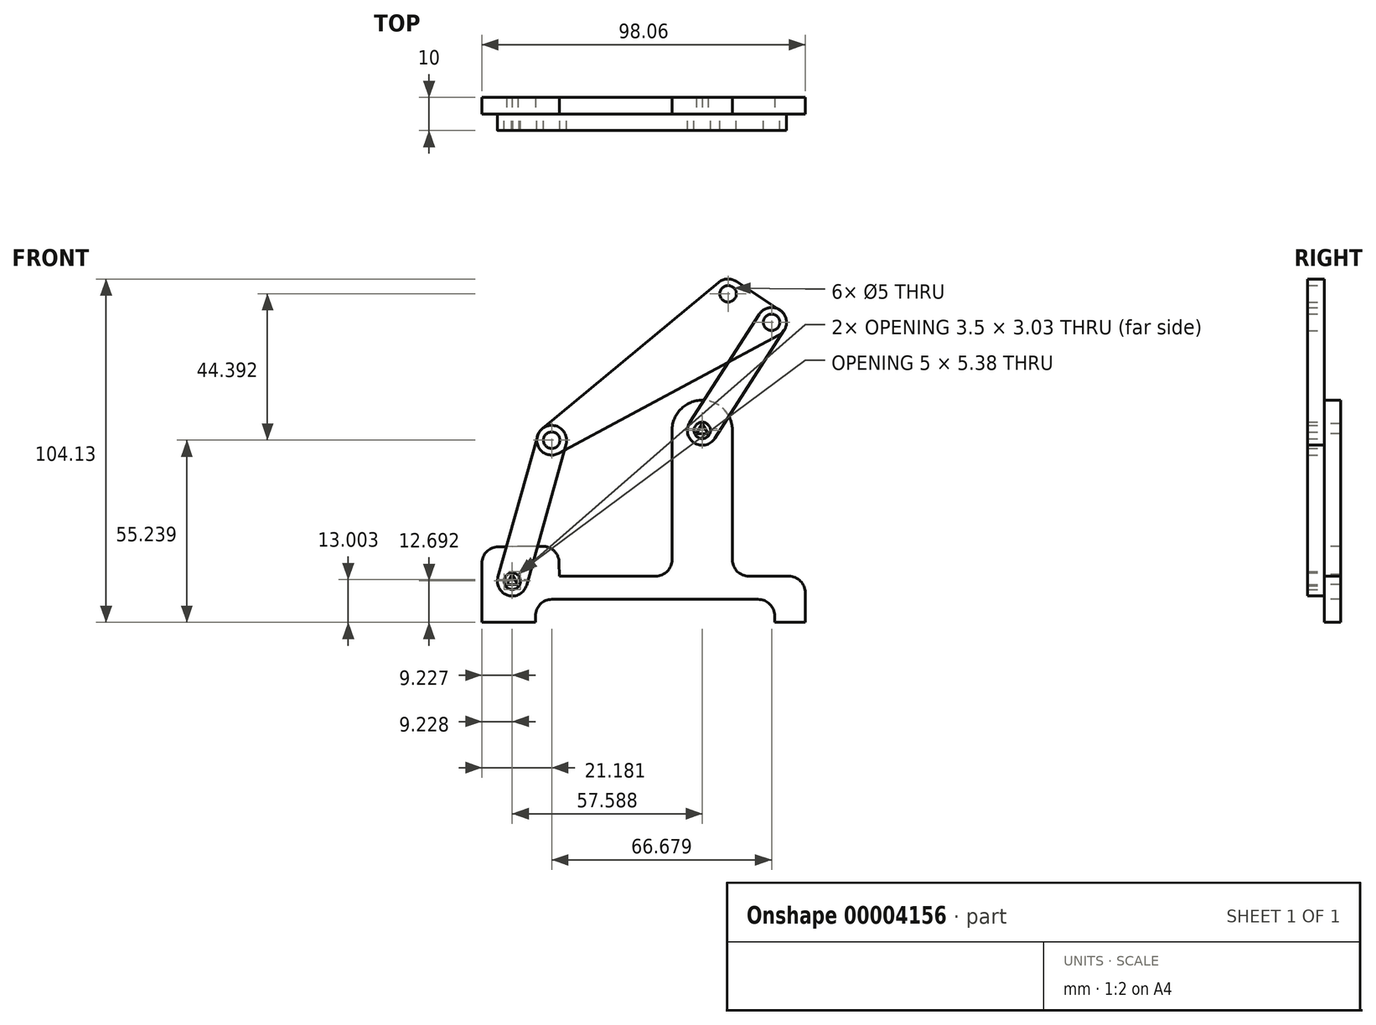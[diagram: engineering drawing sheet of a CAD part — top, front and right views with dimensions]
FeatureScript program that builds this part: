
annotation { "Feature Type Name" : "Feature", "Feature Type Description" : "" }
export const myFeature = defineFeature(function(context is Context, id is Id, definition is map)
    precondition{}
    {
        {
            var Q0;
            Q0=qCreatedBy(makeId("Front.planeOp"),FACE);
            var sketch = newSketch(context, id + "F0", { "sketchPlane" : qUnion([Q0])});
            skLineSegment(sketch, "E0", {"start": v(0, 0) * mm, "end": v(16.8, 0) * mm, "construction": true});
            skLineSegment(sketch, "E1", {"start": v(16.8, 0) * mm, "end": v(16.8, 25.09) * mm, "construction": true});
            skPoint(sketch, "E2", {"position": v(16.8, 25.09) * mm});
            skLineSegment(sketch, "E3", {"start": v(0, 0) * mm, "end": v(43.91, 0) * mm, "construction": true});
            skLineSegment(sketch, "E4", {"start": v(43.91, 0) * mm, "end": v(43.91, 53.03) * mm, "construction": true});
            skPoint(sketch, "E5", {"position": v(43.91, 53.03) * mm});
            skLineSegment(sketch, "E6", {"start": v(0, 0) * mm, "end": v(-40.78, 0) * mm, "construction": true});
            skLineSegment(sketch, "E7", {"start": v(-40.78, -20.63) * mm, "end": v(-40.78, 0) * mm, "construction": true});
            skLineSegment(sketch, "E8", {"start": v(0, 0) * mm, "end": v(-24.45, 0) * mm, "construction": true});
            skLineSegment(sketch, "E9", {"start": v(-24.45, 20.63) * mm, "end": v(-24.45, 0) * mm, "construction": true});
            skLineSegment(sketch, "E10", {"start": v(0, 0) * mm, "end": v(31.16, 0) * mm, "construction": true});
            skLineSegment(sketch, "E11", {"start": v(31.16, 0) * mm, "end": v(31.16, 62.33) * mm, "construction": true});
            skPoint(sketch, "E12", {"position": v(31.16, 62.33) * mm});
            skPoint(sketch, "E13", {"position": v(-24.45, 20.63) * mm});
            skPoint(sketch, "E14", {"position": v(-40.78, -20.63) * mm});
            skSolve(sketch);
        }
        {
            var Q0;
            Q0=qCreatedBy(makeId("Front.planeOp"),FACE);
            var sketch = newSketch(context, id + "F1", { "sketchPlane" : qUnion([Q0])});
            skPoint(sketch, "E15.0", {"position": v(31.16, 62.33) * mm});
            skPoint(sketch, "E16.0", {"position": v(43.91, 53.03) * mm});
            skPoint(sketch, "E17.0", {"position": v(16.8, 25.09) * mm});
            skPoint(sketch, "E18.0", {"position": v(-24.45, 20.63) * mm});
            skPoint(sketch, "E19.0", {"position": v(-40.78, -20.63) * mm});
            skCircle(sketch, "E20", {"center": v(43.91, 53.03) * mm, "radius": 5 * mm});
            skCircle(sketch, "E21", {"center": v(31.16, 62.33) * mm, "radius": 5 * mm});
            skCircle(sketch, "E22", {"center": v(16.8, 25.09) * mm, "radius": 5 * mm});
            skCircle(sketch, "E23", {"center": v(-24.45, 20.63) * mm, "radius": 5 * mm});
            skCircle(sketch, "E24", {"center": v(-40.78, -20.63) * mm, "radius": 5 * mm});
            skCircle(sketch, "E25", {"center": v(-40.78, -20.63) * mm, "radius": 3 * mm});
            skCircle(sketch, "E26", {"center": v(-24.45, 20.63) * mm, "radius": 3 * mm});
            skCircle(sketch, "E27", {"center": v(16.8, 25.09) * mm, "radius": 3 * mm});
            skCircle(sketch, "E28", {"center": v(43.91, 53.03) * mm, "radius": 3 * mm});
            skCircle(sketch, "E29", {"center": v(31.16, 62.33) * mm, "radius": 3 * mm});
            skLineSegment(sketch, "E30", {"start": v(46.86, 57.07) * mm, "end": v(34.1, 66.37) * mm});
            skLineSegment(sketch, "E31", {"start": v(28.16, 66.33) * mm, "end": v(-27.45, 24.63) * mm});
            skLineSegment(sketch, "E32", {"start": v(46.06, 48.51) * mm, "end": v(-22.3, 16.11) * mm});
            skLineSegment(sketch, "E33", {"start": v(20.4, 21.6) * mm, "end": v(47.5, 49.55) * mm});
            skLineSegment(sketch, "E34", {"start": v(40.33, 56.51) * mm, "end": v(13.22, 28.57) * mm});
            skLineSegment(sketch, "E35", {"start": v(-19.8, 18.8) * mm, "end": v(-36.13, -22.47) * mm});
            skLineSegment(sketch, "E36", {"start": v(-29.1, 22.47) * mm, "end": v(-46.2, -20.74) * mm});
            skCircle(sketch, "E37.0", {"center": v(16.8, 25.09) * mm, "radius": 10 * mm});
            skCircle(sketch, "E38.0", {"center": v(-24.45, 20.63) * mm, "radius": 10 * mm});
            skLineSegment(sketch, "E39", {"start": v(17.65, 35.05) * mm, "end": v(-25.48, 30.58) * mm});
            skLineSegment(sketch, "E40", {"start": v(25.88, 29.3) * mm, "end": v(52.76, -28.66) * mm});
            skLineSegment(sketch, "E41", {"start": v(48.23, -35.77) * mm, "end": v(-67.2, -35.77) * mm});
            skLineSegment(sketch, "E42", {"start": v(-71.28, -27.87) * mm, "end": v(-32.6, 26.44) * mm});
            skPoint(sketch, "E43.visualSharp", {"position": v(56.06, -35.77) * mm});
            skArc(sketch, "E43.filletArc", {"start": v(48.23, -35.77) * mm, "mid": v(52.44, -33.46) * mm, "end": v(52.76, -28.66) * mm});
            skPoint(sketch, "E44.visualSharp", {"position": v(-76.9, -35.77) * mm});
            skArc(sketch, "E44.filletArc", {"start": v(-71.28, -27.87) * mm, "mid": v(-71.65, -33.06) * mm, "end": v(-67.2, -35.77) * mm});
            skSolve(sketch);
        }
        {
            var Q0;
            Q0=qCreatedBy(makeId("Front.planeOp"),FACE);
            var sketch = newSketch(context, id + "F2", { "sketchPlane" : qUnion([Q0])});
            skPoint(sketch, "E45.0", {"position": v(24.65, 66.5) * mm});
            skPoint(sketch, "E46.0", {"position": v(37.85, 57.84) * mm});
            skPoint(sketch, "E47.0", {"position": v(16.8, 25.09) * mm});
            skPoint(sketch, "E48.0", {"position": v(-40.78, -20.63) * mm});
            skLineSegment(sketch, "E49", {"start": v(37.85, 57.84) * mm, "end": v(24.65, 66.5) * mm, "construction": true});
            skLineSegment(sketch, "E50", {"start": v(24.65, 66.5) * mm, "end": v(-28.83, 22.1) * mm, "construction": true});
            skLineSegment(sketch, "E51", {"start": v(-28.83, 22.1) * mm, "end": v(37.85, 57.84) * mm, "construction": true});
            skLineSegment(sketch, "E52", {"start": v(37.85, 57.84) * mm, "end": v(16.8, 25.09) * mm, "construction": true});
            skLineSegment(sketch, "E53", {"start": v(-28.83, 22.1) * mm, "end": v(-40.78, -20.63) * mm, "construction": true});
            skSolve(sketch);
        }
        {
            var Q0;
            Q0=qCreatedBy(makeId("Front.planeOp"),FACE);
            var sketch = newSketch(context, id + "F3", { "sketchPlane" : qUnion([Q0])});
            skPoint(sketch, "E54.0", {"position": v(16.8, 25.09) * mm});
            skPoint(sketch, "E55.0", {"position": v(24.65, 66.5) * mm});
            skPoint(sketch, "E56.0", {"position": v(-28.83, 22.1) * mm});
            skPoint(sketch, "E57.0", {"position": v(-40.78, -20.63) * mm});
            skCircle(sketch, "E58", {"center": v(24.65, 66.5) * mm, "radius": 2.5 * mm});
            skCircle(sketch, "E59", {"center": v(24.65, 66.5) * mm, "radius": 4.5 * mm});
            skCircle(sketch, "E60", {"center": v(-28.83, 22.1) * mm, "radius": 4.5 * mm});
            skCircle(sketch, "E61", {"center": v(-28.83, 22.1) * mm, "radius": 2.5 * mm});
            skCircle(sketch, "E62", {"center": v(-40.78, -20.63) * mm, "radius": 2.5 * mm});
            skCircle(sketch, "E63", {"center": v(16.8, 25.09) * mm, "radius": 2.5 * mm});
            skPoint(sketch, "E64.0", {"position": v(37.85, 57.84) * mm});
            skCircle(sketch, "E65", {"center": v(37.85, 57.84) * mm, "radius": 2.5 * mm});
            skCircle(sketch, "E66", {"center": v(37.85, 57.84) * mm, "radius": 4.5 * mm});
            skCircle(sketch, "E67", {"center": v(16.8, 25.09) * mm, "radius": 4.5 * mm});
            skCircle(sketch, "E68", {"center": v(-40.78, -20.63) * mm, "radius": 4.5 * mm});
            skLineSegment(sketch, "E69", {"start": v(48.05, -33.13) * mm, "end": v(38.76, -33.13) * mm});
            skLineSegment(sketch, "E70", {"start": v(38.76, -33.13) * mm, "end": v(38.76, -31.13) * mm});
            skLineSegment(sketch, "E71", {"start": v(33.76, -26.13) * mm, "end": v(-28.76, -26.13) * mm});
            skLineSegment(sketch, "E72", {"start": v(-33.76, -31.13) * mm, "end": v(-33.76, -33.13) * mm});
            skLineSegment(sketch, "E73.trimOffspring", {"start": v(-33.76, -33.13) * mm, "end": v(-50.01, -33.13) * mm});
            skLineSegment(sketch, "E74", {"start": v(-24.5, 20.9) * mm, "end": v(-36.45, -21.84) * mm});
            skLineSegment(sketch, "E75", {"start": v(-33.16, 23.32) * mm, "end": v(-45.12, -19.42) * mm});
            skLineSegment(sketch, "E76", {"start": v(-26.7, 18.14) * mm, "end": v(39.97, 53.87) * mm});
            skLineSegment(sketch, "E77", {"start": v(21.78, 69.96) * mm, "end": v(-31.7, 25.57) * mm});
            skLineSegment(sketch, "E78", {"start": v(40.32, 61.6) * mm, "end": v(27.12, 70.26) * mm});
            skLineSegment(sketch, "E79", {"start": v(41.64, 55.4) * mm, "end": v(20.6, 22.65) * mm});
            skLineSegment(sketch, "E80", {"start": v(34.06, 60.27) * mm, "end": v(13.02, 27.52) * mm});
            skPoint(sketch, "E81.visualSharp", {"position": v(38.76, -26.13) * mm});
            skArc(sketch, "E81.filletArc", {"start": v(38.76, -31.13) * mm, "mid": v(37.3, -27.6) * mm, "end": v(33.76, -26.13) * mm});
            skPoint(sketch, "E82.visualSharp", {"position": v(-33.76, -26.13) * mm});
            skArc(sketch, "E82.filletArc", {"start": v(-28.76, -26.13) * mm, "mid": v(-32.3, -27.6) * mm, "end": v(-33.76, -31.13) * mm});
            skLineSegment(sketch, "E83", {"start": v(-45.06, -10.2) * mm, "end": v(-31.62, -10.06) * mm});
            skLineSegment(sketch, "E84", {"start": v(-26.57, -15.01) * mm, "end": v(-26.53, -19.12) * mm});
            skLineSegment(sketch, "E85", {"start": v(-26.53, -19.12) * mm, "end": v(2.66, -19.12) * mm});
            skLineSegment(sketch, "E86", {"start": v(7.66, -14.12) * mm, "end": v(7.66, 25.09) * mm});
            skLineSegment(sketch, "E87", {"start": v(25.95, 25.09) * mm, "end": v(25.95, -14.12) * mm});
            skLineSegment(sketch, "E88", {"start": v(30.95, -19.12) * mm, "end": v(43.05, -19.12) * mm});
            skArc(sketch, "E89", {"start": v(25.95, 25.09) * mm, "mid": v(16.8, 34.23) * mm, "end": v(7.66, 25.09) * mm});
            skPoint(sketch, "E90.visualSharp", {"position": v(-26.62, -10.01) * mm});
            skArc(sketch, "E90.filletArc", {"start": v(-26.57, -15.01) * mm, "mid": v(-28.07, -11.5) * mm, "end": v(-31.62, -10.06) * mm});
            skLineSegment(sketch, "E91", {"start": v(-50.01, -15.2) * mm, "end": v(-50.01, -33.13) * mm});
            skLineSegment(sketch, "E92", {"start": v(48.05, -24.12) * mm, "end": v(48.05, -33.13) * mm});
            skPoint(sketch, "E93.visualSharp", {"position": v(48.05, -19.12) * mm});
            skArc(sketch, "E93.filletArc", {"start": v(48.05, -24.12) * mm, "mid": v(46.59, -20.58) * mm, "end": v(43.05, -19.12) * mm});
            skPoint(sketch, "E94.visualSharp", {"position": v(-50.01, -10.25) * mm});
            skArc(sketch, "E94.filletArc", {"start": v(-45.06, -10.2) * mm, "mid": v(-48.57, -11.68) * mm, "end": v(-50.01, -15.2) * mm});
            skPoint(sketch, "E95.visualSharp", {"position": v(25.95, -19.12) * mm});
            skArc(sketch, "E95.filletArc", {"start": v(25.95, -14.12) * mm, "mid": v(27.41, -17.65) * mm, "end": v(30.95, -19.12) * mm});
            skPoint(sketch, "E96.visualSharp", {"position": v(7.66, -19.12) * mm});
            skArc(sketch, "E96.filletArc", {"start": v(2.66, -19.12) * mm, "mid": v(6.2, -17.65) * mm, "end": v(7.66, -14.12) * mm});
            skLineSegment(sketch, "E97", {"start": v(-38.28, -22.08) * mm, "end": v(-43.28, -22.08) * mm});
            skLineSegment(sketch, "E98", {"start": v(-43.28, -22.08) * mm, "end": v(-40.78, -17.75) * mm});
            skLineSegment(sketch, "E99", {"start": v(-40.78, -17.75) * mm, "end": v(-38.28, -22.08) * mm});
            skLineSegment(sketch, "E100", {"start": v(-40.78, -22.08) * mm, "end": v(-40.78, -17.75) * mm, "construction": true});
            skLineSegment(sketch, "E101", {"start": v(-39.53, -19.91) * mm, "end": v(-43.28, -22.08) * mm, "construction": true});
            skLineSegment(sketch, "E102", {"start": v(-42.03, -19.91) * mm, "end": v(-38.28, -22.08) * mm, "construction": true});
            skSolve(sketch);
        }
        {
            var Q0;
            Q0=qCreatedBy(makeId("Front.planeOp"),FACE);
            var sketch = newSketch(context, id + "F4", { "sketchPlane" : qUnion([Q0])});
            skArc(sketch, "E103.0", {"start": v(-45.06, -10.2) * mm, "mid": v(-48.57, -11.68) * mm, "end": v(-50.01, -15.2) * mm});
            skArc(sketch, "E103.2", {"start": v(-26.57, -15.01) * mm, "mid": v(-28.07, -11.5) * mm, "end": v(-31.62, -10.06) * mm});
            skLineSegment(sketch, "E103.3", {"start": v(-26.57, -15.01) * mm, "end": v(-26.53, -19.12) * mm});
            skLineSegment(sketch, "E104.0.0", {"start": v(48.05, -33.13) * mm, "end": v(38.76, -33.13) * mm});
            skLineSegment(sketch, "E104.0.1", {"start": v(48.05, -24.12) * mm, "end": v(48.05, -33.13) * mm});
            skArc(sketch, "E104.0.2", {"start": v(48.05, -24.12) * mm, "mid": v(46.59, -20.58) * mm, "end": v(43.05, -19.12) * mm});
            skLineSegment(sketch, "E104.0.3", {"start": v(30.95, -19.12) * mm, "end": v(43.05, -19.12) * mm});
            skArc(sketch, "E104.0.4", {"start": v(25.95, -14.12) * mm, "mid": v(27.41, -17.65) * mm, "end": v(30.95, -19.12) * mm});
            skLineSegment(sketch, "E104.0.5", {"start": v(25.95, 25.09) * mm, "end": v(25.95, -14.12) * mm});
            skLineSegment(sketch, "E104.0.11", {"start": v(7.66, -14.12) * mm, "end": v(7.66, 25.09) * mm});
            skArc(sketch, "E104.0.12", {"start": v(2.66, -19.12) * mm, "mid": v(6.2, -17.65) * mm, "end": v(7.66, -14.12) * mm});
            skLineSegment(sketch, "E104.0.13", {"start": v(-26.53, -19.12) * mm, "end": v(2.66, -19.12) * mm});
            skLineSegment(sketch, "E104.0.22", {"start": v(-50.01, -15.2) * mm, "end": v(-50.01, -33.13) * mm});
            skLineSegment(sketch, "E104.0.23", {"start": v(-33.76, -33.13) * mm, "end": v(-50.01, -33.13) * mm});
            skLineSegment(sketch, "E104.0.24", {"start": v(-33.76, -31.13) * mm, "end": v(-33.76, -33.13) * mm});
            skArc(sketch, "E104.0.25", {"start": v(-28.76, -26.13) * mm, "mid": v(-32.3, -27.6) * mm, "end": v(-33.76, -31.13) * mm});
            skLineSegment(sketch, "E104.0.26", {"start": v(33.76, -26.13) * mm, "end": v(-28.76, -26.13) * mm});
            skArc(sketch, "E104.0.27", {"start": v(38.76, -31.13) * mm, "mid": v(37.3, -27.6) * mm, "end": v(33.76, -26.13) * mm});
            skLineSegment(sketch, "E104.0.28", {"start": v(38.76, -33.13) * mm, "end": v(38.76, -31.13) * mm});
            skArc(sketch, "E105.0", {"start": v(25.95, 25.09) * mm, "mid": v(16.8, 34.23) * mm, "end": v(7.66, 25.09) * mm});
            skPoint(sketch, "E106", {"position": v(-40.78, -20.63) * mm});
            skLineSegment(sketch, "E107", {"start": v(-31.62, -10.06) * mm, "end": v(-45.06, -10.2) * mm});
            skLineSegment(sketch, "E108", {"start": v(-39.03, -21.64) * mm, "end": v(-42.53, -21.64) * mm});
            skLineSegment(sketch, "E109", {"start": v(-42.53, -21.64) * mm, "end": v(-40.78, -18.61) * mm});
            skLineSegment(sketch, "E110", {"start": v(-40.78, -18.61) * mm, "end": v(-39.03, -21.64) * mm});
            skLineSegment(sketch, "E111", {"start": v(-39.9, -20.13) * mm, "end": v(-42.53, -21.64) * mm, "construction": true});
            skLineSegment(sketch, "E112", {"start": v(-41.66, -20.13) * mm, "end": v(-39.03, -21.64) * mm, "construction": true});
            skLineSegment(sketch, "E113", {"start": v(-40.78, -18.61) * mm, "end": v(-40.78, -21.64) * mm, "construction": true});
            skLineSegment(sketch, "E114", {"start": v(18.56, 24.08) * mm, "end": v(15.06, 24.08) * mm});
            skLineSegment(sketch, "E115", {"start": v(15.06, 24.08) * mm, "end": v(16.8, 27.1) * mm});
            skLineSegment(sketch, "E116", {"start": v(16.8, 27.1) * mm, "end": v(18.56, 24.08) * mm});
            skLineSegment(sketch, "E117", {"start": v(16.8, 27.1) * mm, "end": v(16.8, 24.08) * mm, "construction": true});
            skLineSegment(sketch, "E118", {"start": v(17.68, 25.6) * mm, "end": v(15.06, 24.08) * mm, "construction": true});
            skLineSegment(sketch, "E119", {"start": v(15.93, 25.6) * mm, "end": v(18.56, 24.08) * mm, "construction": true});
            skSolve(sketch);
        }
        {
            var Q0;
            Q0=makeQuery(id+"F4.imprint","IMPRINT",FACE,{"disambiguationData":[TD([[makeQuery(id+"F4.imprint","IMPRINT",EDGE,{"derivedFrom":sQuery(id+"F4.wireOp",EDGE,"E104.0.0")}),-1.0]])]});
            extrude(context, id + "F5", {"entities" : qUnion([Q0]), "oppositeDirection" : true, "depth" : 5 * mm});
        }
        {
            var Q0;
            {var subQ3=sQuery(id+"F3.wireOp",EDGE,"E75");var subQ7=sQuery(id+"F3.wireOp",EDGE,"E60");var subQ9=makeQuery(id+"F3.imprint","INTERSECT",VERTEX,{"derivedFrom":[subQ7,subQ3]});Q0=makeQuery(id+"F3.imprint","IMPRINT",FACE,{"disambiguationData":[TD([[makeQuery(id+"F3.imprint","IMPRINT",EDGE,{"disambiguationData":[TD([[subQ9,-1.0]])],"derivedFrom":subQ7}),-1.0]])]});}
            var Q1;
            {var subQ1=sQuery(id+"F3.wireOp",EDGE,"E74");var subQ5=sQuery(id+"F3.wireOp",EDGE,"E68");var subQ7=makeQuery(id+"F3.imprint","INTERSECT",VERTEX,{"derivedFrom":[subQ5,subQ1]});Q1=makeQuery(id+"F3.imprint","IMPRINT",FACE,{"disambiguationData":[TD([[makeQuery(id+"F3.imprint","IMPRINT",EDGE,{"disambiguationData":[TD([[subQ7,-1.0]])],"derivedFrom":subQ5}),-1.0]])]});}
            var Q2;
            {var subQ1=sQuery(id+"F3.wireOp",EDGE,"E62");var subQ5=sQuery(id+"F3.wireOp",EDGE,"E98");var subQ15=makeQuery(id+"F3.imprint","INTERSECT",VERTEX,{"disambiguationData":[OD(0.0)],"derivedFrom":[subQ1,subQ5]});Q2=makeQuery(id+"F3.imprint","IMPRINT",FACE,{"disambiguationData":[TD([[makeQuery(id+"F3.imprint","IMPRINT",EDGE,{"disambiguationData":[TD([[subQ15,-1.0]])],"derivedFrom":subQ1}),-1.0]])]});}
            var Q3;
            Q3=makeQuery(id+"F3.imprint","IMPRINT",FACE,{"disambiguationData":[TD([[makeQuery(id+"F3.imprint","IMPRINT",EDGE,{"derivedFrom":sQuery(id+"F3.wireOp",EDGE,"E61")}),-1.0]])]});
            var Q4;
            {var subQ1=sQuery(id+"F3.wireOp",EDGE,"E74");var subQ3=sQuery(id+"F3.wireOp",EDGE,"E60");var subQ5=makeQuery(id+"F3.imprint","INTERSECT",VERTEX,{"derivedFrom":[subQ3,subQ1]});Q4=makeQuery(id+"F3.imprint","IMPRINT",FACE,{"disambiguationData":[TD([[makeQuery(id+"F3.imprint","IMPRINT",EDGE,{"disambiguationData":[TD([[subQ5,1.0]])],"derivedFrom":subQ3}),-1.0]])]});}
            var Q5;
            {var subQ1=sQuery(id+"F3.wireOp",EDGE,"E62");var subQ3=sQuery(id+"F3.wireOp",EDGE,"E97");var subQ5=makeQuery(id+"F3.imprint","INTERSECT",VERTEX,{"disambiguationData":[OD(1.0)],"derivedFrom":[subQ1,subQ3]});Q5=makeQuery(id+"F3.imprint","IMPRINT",FACE,{"disambiguationData":[TD([[makeQuery(id+"F3.imprint","IMPRINT",EDGE,{"disambiguationData":[TD([[subQ5,-1.0]])],"derivedFrom":subQ1}),-1.0]])]});}
            var Q6;
            {var subQ1=sQuery(id+"F3.wireOp",EDGE,"E62");var subQ3=sQuery(id+"F3.wireOp",EDGE,"E98");var subQ5=makeQuery(id+"F3.imprint","INTERSECT",VERTEX,{"disambiguationData":[OD(0.0)],"derivedFrom":[subQ1,subQ3]});Q6=makeQuery(id+"F3.imprint","IMPRINT",FACE,{"disambiguationData":[TD([[makeQuery(id+"F3.imprint","IMPRINT",EDGE,{"disambiguationData":[TD([[subQ5,1.0]])],"derivedFrom":subQ1}),-1.0]])]});}
            var Q7;
            {var subQ0=sQuery(id+"F3.wireOp",EDGE,"E98");var subQ1=sQuery(id+"F3.wireOp",EDGE,"E62");var subQ2=makeQuery(id+"F3.imprint","INTERSECT",VERTEX,{"disambiguationData":[OD(1.0)],"derivedFrom":[subQ1,subQ0]});Q7=makeQuery(id+"F3.imprint","IMPRINT",FACE,{"disambiguationData":[TD([[makeQuery(id+"F3.imprint","IMPRINT",EDGE,{"disambiguationData":[TD([[subQ2,-1.0]])],"derivedFrom":subQ1}),-1.0]])]});}
            extrude(context, id + "F6", {"entities" : qUnion([Q0, Q1, Q2, Q3, Q4, Q5, Q6, Q7]), "depth" : 5 * mm});
        }
        {
            var Q0;
            {var subQ1=sQuery(id+"F3.wireOp",EDGE,"E76");var subQ3=sQuery(id+"F3.wireOp",EDGE,"E66");var subQ5=makeQuery(id+"F3.imprint","INTERSECT",VERTEX,{"derivedFrom":[subQ3,subQ1]});Q0=makeQuery(id+"F3.imprint","IMPRINT",FACE,{"disambiguationData":[TD([[makeQuery(id+"F3.imprint","IMPRINT",EDGE,{"disambiguationData":[TD([[subQ5,1.0]])],"derivedFrom":subQ3}),-1.0]])]});}
            var Q1;
            {var subQ5=sQuery(id+"F3.wireOp",EDGE,"E76");var subQ7=sQuery(id+"F3.wireOp",EDGE,"E66");var subQ8=makeQuery(id+"F3.imprint","INTERSECT",VERTEX,{"derivedFrom":[subQ7,subQ5]});Q1=makeQuery(id+"F3.imprint","IMPRINT",FACE,{"disambiguationData":[TD([[makeQuery(id+"F3.imprint","IMPRINT",EDGE,{"disambiguationData":[TD([[subQ8,-1.0]])],"derivedFrom":subQ7}),-1.0]])]});}
            var Q2;
            Q2=makeQuery(id+"F3.imprint","IMPRINT",FACE,{"disambiguationData":[TD([[makeQuery(id+"F3.imprint","IMPRINT",EDGE,{"derivedFrom":sQuery(id+"F3.wireOp",EDGE,"E65")}),-1.0]])]});
            var Q3;
            {var subQ3=sQuery(id+"F3.wireOp",EDGE,"E67");var subQ5=sQuery(id+"F3.wireOp",EDGE,"E79");var subQ7=makeQuery(id+"F3.imprint","INTERSECT",VERTEX,{"derivedFrom":[subQ3,subQ5]});Q3=makeQuery(id+"F3.imprint","IMPRINT",FACE,{"disambiguationData":[TD([[makeQuery(id+"F3.imprint","IMPRINT",EDGE,{"disambiguationData":[TD([[subQ7,-1.0]])],"derivedFrom":subQ3}),-1.0]])]});}
            var Q4;
            Q4=makeQuery(id+"F3.imprint","IMPRINT",FACE,{"disambiguationData":[TD([[makeQuery(id+"F3.imprint","IMPRINT",EDGE,{"derivedFrom":sQuery(id+"F3.wireOp",EDGE,"E63")}),-1.0]])]});
            extrude(context, id + "F7", {"entities" : qUnion([Q0, Q1, Q2, Q3, Q4]), "depth" : 5 * mm});
        }
        {
            var Q0;
            {var subQ6=sQuery(id+"F3.wireOp",EDGE,"E77");Q0=makeQuery(id+"F3.imprint","IMPRINT",FACE,{"disambiguationData":[TD([[makeQuery(id+"F3.imprint","IMPRINT",EDGE,{"derivedFrom":subQ6}),1.0]])]});}
            var Q1;
            Q1=makeQuery(id+"F3.imprint","IMPRINT",FACE,{"disambiguationData":[TD([[makeQuery(id+"F3.imprint","IMPRINT",EDGE,{"derivedFrom":sQuery(id+"F3.wireOp",EDGE,"E58")}),-1.0]])]});
            var Q2;
            {var subQ1=sQuery(id+"F3.wireOp",EDGE,"E76");var subQ3=sQuery(id+"F3.wireOp",EDGE,"E66");var subQ5=makeQuery(id+"F3.imprint","INTERSECT",VERTEX,{"derivedFrom":[subQ3,subQ1]});Q2=makeQuery(id+"F3.imprint","IMPRINT",FACE,{"disambiguationData":[TD([[makeQuery(id+"F3.imprint","IMPRINT",EDGE,{"disambiguationData":[TD([[subQ5,1.0]])],"derivedFrom":subQ3}),-1.0]])]});}
            var Q3;
            Q3=makeQuery(id+"F3.imprint","IMPRINT",FACE,{"disambiguationData":[TD([[makeQuery(id+"F3.imprint","IMPRINT",EDGE,{"derivedFrom":sQuery(id+"F3.wireOp",EDGE,"E65")}),-1.0]])]});
            var Q4;
            Q4=makeQuery(id+"F3.imprint","IMPRINT",FACE,{"disambiguationData":[TD([[makeQuery(id+"F3.imprint","IMPRINT",EDGE,{"derivedFrom":sQuery(id+"F3.wireOp",EDGE,"E61")}),-1.0]])]});
            var Q5;
            {var subQ1=sQuery(id+"F3.wireOp",EDGE,"E74");var subQ3=sQuery(id+"F3.wireOp",EDGE,"E60");var subQ5=makeQuery(id+"F3.imprint","INTERSECT",VERTEX,{"derivedFrom":[subQ3,subQ1]});Q5=makeQuery(id+"F3.imprint","IMPRINT",FACE,{"disambiguationData":[TD([[makeQuery(id+"F3.imprint","IMPRINT",EDGE,{"disambiguationData":[TD([[subQ5,1.0]])],"derivedFrom":subQ3}),-1.0]])]});}
            extrude(context, id + "F8", {"entities" : qUnion([Q0, Q1, Q2, Q3, Q4, Q5]), "depth" : 5 * mm});
        }
    });
